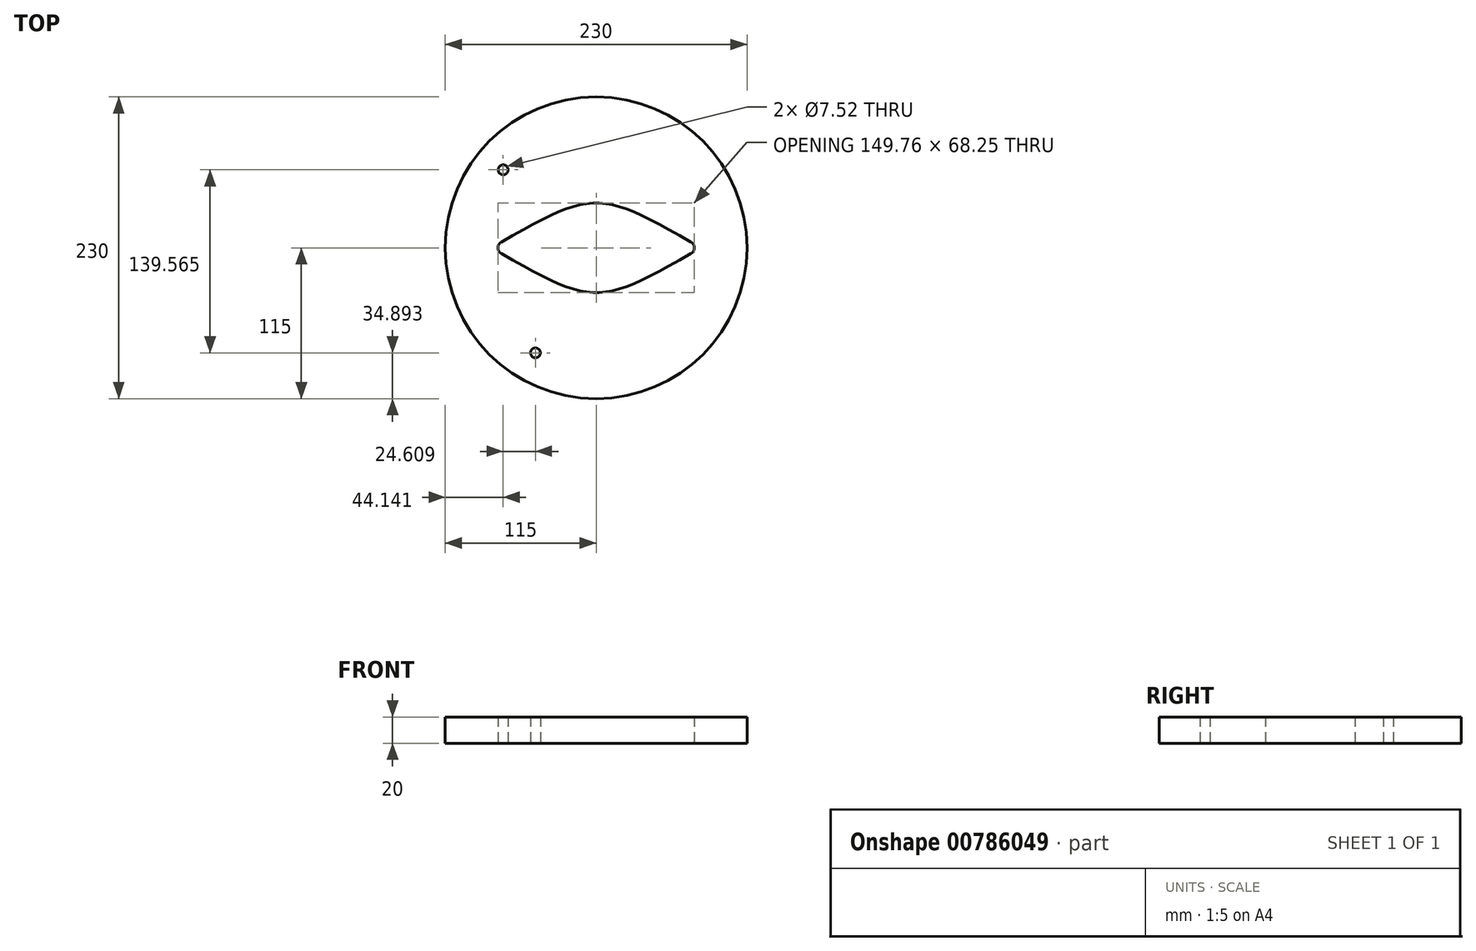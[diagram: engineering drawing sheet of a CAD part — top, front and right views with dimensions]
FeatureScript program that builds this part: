
annotation { "Feature Type Name" : "Feature", "Feature Type Description" : "" }
export const myFeature = defineFeature(function(context is Context, id is Id, definition is map)
    precondition{}
    {
        {
            var Q0;
            Q0=qCreatedBy(makeId("Top.planeOp"),FACE);
            var sketch = newSketch(context, id + "F0", { "sketchPlane" : qUnion([Q0])});
            skCircle(sketch, "E0", {"center": v(0, 0) * mm, "radius": 115 * mm});
            skLineSegment(sketch, "E1", {"start": v(-80, 0) * mm, "end": v(80, 0) * mm, "construction": true});
            skFitSpline(sketch, "E2", {"points": [v(-80, 0) * mm, v(80, 0) * mm], "startDerivative": vector(240, 136.5) * mm, "endDerivative": vector(240, -136.5) * mm});
            skFitSpline(sketch, "E3.MirrorCS", {"points": [v(-80, 0) * mm, v(80, 0) * mm], "startDerivative": vector(240, -136.5) * mm, "endDerivative": vector(240, 136.5) * mm});
            skSolve(sketch);
        }
        {
            var Q0;
            Q0=qSketchRegion(id+"F0",true);
            extrude(context, id + "F1", {"entities" : qUnion([Q0]), "depth" : 20 * mm});
        }
        {
            var Q0;
            {var subQ0=sQuery(id+"F0.wireOp",EDGE,"E3.MirrorCS");var subQ1=sQuery(id+"F0.wireOp",EDGE,"E2");Q0=makeQuery(id+"F1.opExtrude","SWEPT_EDGE",EDGE,{"disambiguationData":[OSD([subQ1,subQ0]),TDD([makeQuery(id+"F0.imprint","INTERSECT",VERTEX,{"disambiguationData":[OD(0.0)],"derivedFrom":[subQ1,subQ0]})])]});}
            var Q1;
            {var subQ0=sQuery(id+"F0.wireOp",EDGE,"E3.MirrorCS");var subQ1=sQuery(id+"F0.wireOp",EDGE,"E2");Q1=makeQuery(id+"F1.opExtrude","SWEPT_EDGE",EDGE,{"disambiguationData":[OSD([subQ1,subQ0]),TDD([makeQuery(id+"F0.imprint","INTERSECT",VERTEX,{"disambiguationData":[OD(1.0)],"derivedFrom":[subQ1,subQ0]})])]});}
            fillet(context, id + "F2", {"entities" : qUnion([Q0, Q1]), "radius" : 5 * mm, "tangentPropagation" : true, "allowEdgeOverflow" : false});
        }
        {
            var Q0;
            Q0=qCreatedBy(makeId("Top.planeOp"),FACE);
            var sketch = newSketch(context, id + "F3", { "sketchPlane" : qUnion([Q0])});
            skCircle(sketch, "E4", {"center": v(0, 0) * mm, "radius": 92.5 * mm, "construction": true});
            skCircle(sketch, "E5", {"center": v(-70.86, 59.46) * mm, "radius": 3.76 * mm});
            skCircle(sketch, "E6", {"center": v(-46.25, -80.1) * mm, "radius": 3.76 * mm});
            skLineSegment(sketch, "E7", {"start": v(-70.86, 59.46) * mm, "end": v(0, 0) * mm, "construction": true});
            skLineSegment(sketch, "E8", {"start": v(0, 0) * mm, "end": v(-46.25, -80.1) * mm, "construction": true});
            skLineSegment(sketch, "E9", {"start": v(0, 0) * mm, "end": v(-92.5, 0) * mm, "construction": true});
            skLineSegment(sketch, "E10", {"start": v(0, 92.5) * mm, "end": v(0, -92.5) * mm, "construction": true});
            skCircle(sketch, "E11", {"center": v(92.5, 0) * mm, "radius": 3.76 * mm, "construction": true});
            skSolve(sketch);
        }
        {
            var Q0;
            Q0=qSketchRegion(id+"F3",true);
            extrude(context, id + "F4", {"entities" : qUnion([Q0]), "operationType" : NewBodyOperationType.REMOVE, "depth" : 25 * mm, "offsetDistance" : 25 * mm});
        }
    });
